# Revit family: MyFlow Sofa
name_source: partatom
category: Furniture
units: mm (PartAtom-declared; Revit-internal decimal feet)

## family parameters
Always vertical = Yes
Cut with Voids When Loaded = No
OmniClass Number = 23.40.20.00
OmniClass Title = General Furniture and Specialties
Room Calculation Point = No
Shared = No
Work Plane-Based = No

## types (2) — shared parameters
BackrestInColour = Fabric (Light Grey)
BackrestOutColour = Fabric (Grey)
Depth = 750 mm  [stored 2.46063 ft]
Height = 900 mm  [stored 2.95276 ft]
ManufactureURL = https://www.isku.fi
Manufacturer = ISKU
SeatColour = Fabric (Light Grey)
zero-valued in all types: NorminalDepth, NorminalHeight

## per-type parameters (varying)
| type | LegColour | Model | SofaL | SofaXL | Width |
| Sofa L | Stainless Steel | MyFlow Sofa - Size L | Yes | No | 1750 mm  [stored 5.74147 ft] |
| Sofa XL | <By Category> | MyFlow Sofa - Size XL | No | Yes | 2530 mm  [stored 8.30052 ft] |

note: [stored X ft] marks values corroborated as IEEE doubles in the binary element streams (Revit-internal decimal feet)

## geometry (parser evidence)
native form markers: Sweep x15
no freeform markers — native parametric forms only
